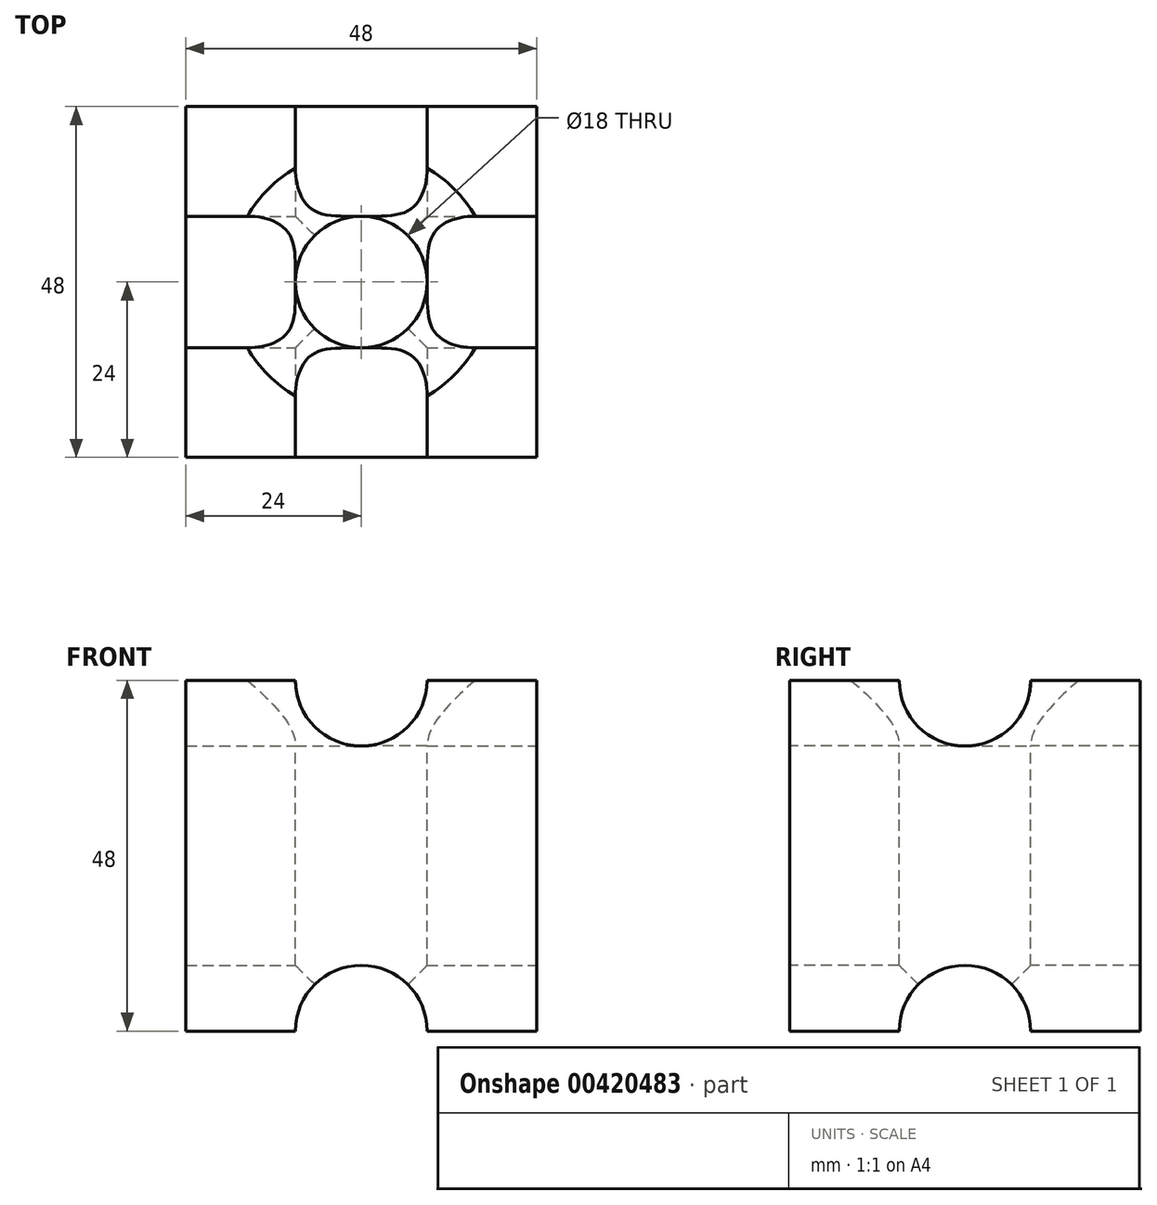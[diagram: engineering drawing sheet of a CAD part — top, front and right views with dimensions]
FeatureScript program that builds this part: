
annotation { "Feature Type Name" : "Feature", "Feature Type Description" : "" }
export const myFeature = defineFeature(function(context is Context, id is Id, definition is map)
    precondition{}
    {
        {
            var Q0;
            Q0=qCreatedBy(makeId("Front.planeOp"),FACE);
            var sketch = newSketch(context, id + "F0", { "sketchPlane" : qUnion([Q0])});
            skLineSegment(sketch, "E0.bottom", {"start": v(-24, 24) * mm, "end": v(24, 24) * mm});
            skLineSegment(sketch, "E0.top", {"start": v(-24, -24) * mm, "end": v(24, -24) * mm});
            skLineSegment(sketch, "E0.left", {"start": v(-24, 24) * mm, "end": v(-24, -24) * mm});
            skLineSegment(sketch, "E0.right", {"start": v(24, 24) * mm, "end": v(24, -24) * mm});
            skPoint(sketch, "E0.middle", {"position": v(0, 0) * mm});
            skSolve(sketch);
        }
        {
            var Q0;
            Q0=makeQuery(id+"F0.imprint","IMPRINT",FACE,{"disambiguationData":[TD([[makeQuery(id+"F0.imprint","IMPRINT",EDGE,{"derivedFrom":sQuery(id+"F0.wireOp",EDGE,"E0.bottom")}),-1.0]])]});
            extrude(context, id + "F1", {"entities" : qUnion([Q0]), "depth" : 48 * mm, "symmetric" : true});
        }
        {
            var Q0;
            Q0=makeQuery(id+"F1.opExtrude","CAP_FACE",FACE,{"disambiguationData":[OSD([sQuery(id+"F0.wireOp",EDGE,"E0.bottom"),sQuery(id+"F0.wireOp",EDGE,"E0.top"),sQuery(id+"F0.wireOp",EDGE,"E0.left"),sQuery(id+"F0.wireOp",EDGE,"E0.right")])],"isStart":false});
            var sketch = newSketch(context, id + "F2", { "sketchPlane" : qUnion([Q0])});
            skCircle(sketch, "E1", {"center": v(0, 24) * mm, "radius": 9 * mm});
            skPoint(sketch, "E2", {"position": v(0, -24) * mm});
            skCircle(sketch, "E3", {"center": v(0, -24) * mm, "radius": 9 * mm});
            skSolve(sketch);
        }
        {
            var Q0;
            Q0=qSketchRegion(id+"F2",true);
            extrude(context, id + "F3", {"entities" : qUnion([Q0]), "operationType" : NewBodyOperationType.REMOVE, "oppositeDirection" : true, "depth" : 48 * mm});
        }
        {
            var Q0;
            Q0=makeQuery(id+"F1.opExtrude","SWEPT_FACE",FACE,{"disambiguationData":[OSD([sQuery(id+"F0.wireOp",EDGE,"E0.right")])]});
            var sketch = newSketch(context, id + "F4", { "sketchPlane" : qUnion([Q0])});
            skCircle(sketch, "E4", {"center": v(0, 24) * mm, "radius": 9 * mm});
            skPoint(sketch, "E5", {"position": v(0, -24) * mm});
            skCircle(sketch, "E6", {"center": v(0, -24) * mm, "radius": 9 * mm});
            skSolve(sketch);
        }
        {
            var Q0;
            Q0=makeQuery(id+"F1.opExtrude","SWEPT_FACE",FACE,{"disambiguationData":[OSD([sQuery(id+"F0.wireOp",EDGE,"E0.bottom")])]});
            var sketch = newSketch(context, id + "F5", { "sketchPlane" : qUnion([Q0])});
            skPoint(sketch, "E7", {"position": v(0, 0) * mm});
            skSolve(sketch);
        }
        {
            var Q0;
            Q0=sQuery(id+"F5.wireOp",VERTEX,"E7");
            var Q1;
            Q1=makeQuery(id+"F1.opExtrude","SWEPT_BODY",BODY,{"disambiguationData":[OSD([sQuery(id+"F0.wireOp",EDGE,"E0.bottom"),sQuery(id+"F0.wireOp",EDGE,"E0.top"),sQuery(id+"F0.wireOp",EDGE,"E0.left"),sQuery(id+"F0.wireOp",EDGE,"E0.right")])]});
            hole(context, id + "F6", {"style" : HoleStyle.C_SINK, "endStyle" : HoleEndStyle.THROUGH, "holeDiameter" : 18 * mm, "cSinkDiameter" : 36 * mm, "cSinkAngle" : 90 * degree, "isTappedThrough" : true, "tappedDepth" : 12 * mm, "tapClearance" : 3, "startFromSketch" : true, "locations" : qUnion([Q0]), "scope" : qUnion([Q1])});
        }
        {
            var Q0;
            Q0 = qSketchRegion(id + "F4", true);
            extrude(context, id + "F7", {"entities" : qUnion([Q0]), "operationType" : NewBodyOperationType.REMOVE, "oppositeDirection" : true, "depth" : 48 * mm});
        }
    });
